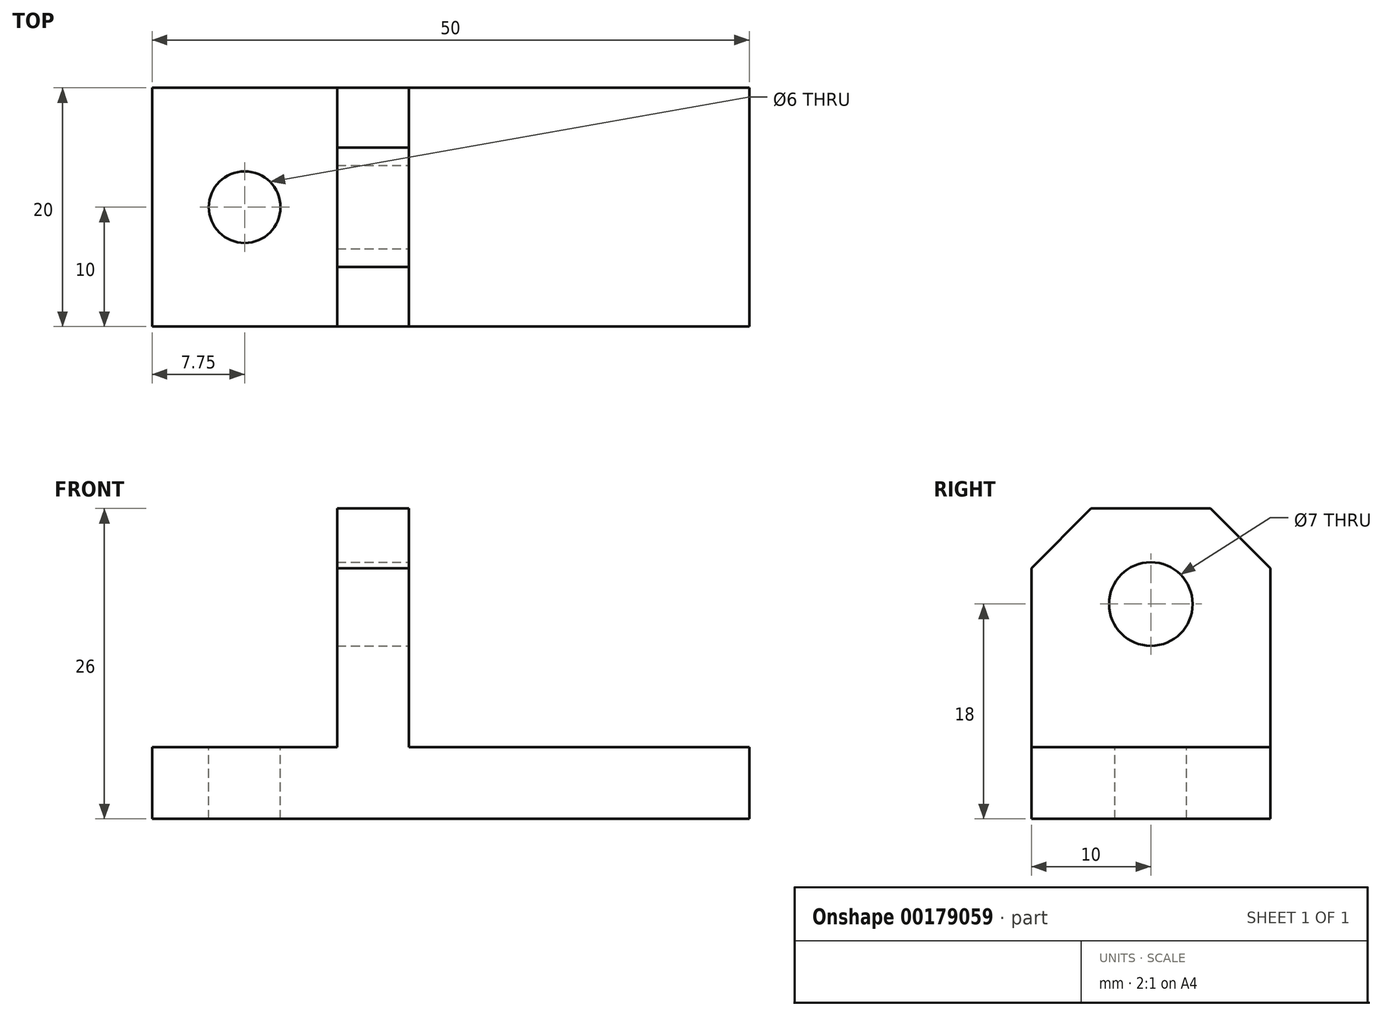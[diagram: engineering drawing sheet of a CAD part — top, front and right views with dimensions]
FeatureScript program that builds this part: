
annotation { "Feature Type Name" : "Feature", "Feature Type Description" : "" }
export const myFeature = defineFeature(function(context is Context, id is Id, definition is map)
    precondition{}
    {
        {
            var Q0;
            Q0=qCreatedBy(makeId("Top.planeOp"),FACE);
            var sketch = newSketch(context, id + "F0", { "sketchPlane" : qUnion([Q0])});
            skLineSegment(sketch, "E0.bottom", {"start": v(25, -10) * mm, "end": v(-25, -10) * mm});
            skLineSegment(sketch, "E0.top", {"start": v(25, 10) * mm, "end": v(-25, 10) * mm});
            skLineSegment(sketch, "E0.left", {"start": v(25, -10) * mm, "end": v(25, 10) * mm});
            skLineSegment(sketch, "E0.right", {"start": v(-25, -10) * mm, "end": v(-25, 10) * mm});
            skPoint(sketch, "E0.middle", {"position": v(0, 0) * mm});
            skSolve(sketch);
        }
        {
            var Q0;
            Q0 = qSketchRegion(id + "F0", true);
            extrude(context, id + "F1", {"entities" : qUnion([Q0]), "depth" : 6 * mm});
        }
        {
            var Q0;
            Q0=makeQuery(id+"F1.opExtrude","CAP_FACE",FACE,{"disambiguationData":[OSD([sQuery(id+"F0.wireOp",EDGE,"E0.bottom"),sQuery(id+"F0.wireOp",EDGE,"E0.top"),sQuery(id+"F0.wireOp",EDGE,"E0.left"),sQuery(id+"F0.wireOp",EDGE,"E0.right")])],"isStart":false});
            var sketch = newSketch(context, id + "F2", { "sketchPlane" : qUnion([Q0])});
            skLineSegment(sketch, "E1", {"start": v(0, 10) * mm, "end": v(0, -10) * mm, "construction": true});
            skLineSegment(sketch, "E2.bottom", {"start": v(-9.5, 10) * mm, "end": v(-3.5, 10) * mm});
            skLineSegment(sketch, "E2.top", {"start": v(-9.5, -10) * mm, "end": v(-3.5, -10) * mm});
            skLineSegment(sketch, "E2.left", {"start": v(-9.5, 10) * mm, "end": v(-9.5, -10) * mm});
            skLineSegment(sketch, "E2.right", {"start": v(-3.5, 10) * mm, "end": v(-3.5, -10) * mm});
            skSolve(sketch);
        }
        {
            var Q0;
            Q0 = qSketchRegion(id + "F2", true);
            extrude(context, id + "F3", {"entities" : qUnion([Q0]), "operationType" : NewBodyOperationType.ADD, "depth" : 20 * mm});
        }
        {
            var Q0;
            Q0=makeQuery(id+"F3.opExtrude","SWEPT_FACE",FACE,{"disambiguationData":[OSD([sQuery(id+"F2.wireOp",EDGE,"E2.right")])]});
            var sketch = newSketch(context, id + "F4", { "sketchPlane" : qUnion([Q0])});
            skLineSegment(sketch, "E3", {"start": v(0, 26) * mm, "end": v(0, 6) * mm, "construction": true});
            skCircle(sketch, "E4", {"center": v(0, 18) * mm, "radius": 3.5 * mm});
            skSolve(sketch);
        }
        {
            var Q0;
            Q0 = qSketchRegion(id + "F4", true);
            extrude(context, id + "F5", {"entities" : qUnion([Q0]), "operationType" : NewBodyOperationType.REMOVE, "oppositeDirection" : true, "depth" : 25 * mm});
        }
        {
            var Q0;
            Q0=makeQuery(id+"F3.opExtrude","CAP_EDGE",EDGE,{"disambiguationData":[OSD([sQuery(id+"F2.wireOp",EDGE,"E2.top")])],"isStart":false});
            var Q1;
            Q1=makeQuery(id+"F3.opExtrude","CAP_EDGE",EDGE,{"disambiguationData":[OSD([sQuery(id+"F2.wireOp",EDGE,"E2.bottom")])],"isStart":false});
            chamfer(context, id + "F6", {"entities" : qUnion([Q0, Q1]), "width" : 5 * mm, "tangentPropagation" : true});
        }
        {
            var Q0;
            {var subQ0=sQuery(id+"F0.wireOp",EDGE,"E0.right");var subQ1=sQuery(id+"F0.wireOp",EDGE,"E0.top");var subQ2=sQuery(id+"F0.wireOp",EDGE,"E0.bottom");Q0=makeQuery(id+"F3.boolean.opBoolean","SPLIT",FACE,{"disambiguationData":[TD([makeQuery(id+"F1.opExtrude","SWEPT_FACE",FACE,{"disambiguationData":[OSD([subQ0])]})])],"derivedFrom":makeQuery(id+"F1.opExtrude","CAP_FACE",FACE,{"disambiguationData":[OSD([subQ2,subQ1,sQuery(id+"F0.wireOp",EDGE,"E0.left"),subQ0])],"isStart":false})});}
            var sketch = newSketch(context, id + "F7", { "sketchPlane" : qUnion([Q0])});
            skLineSegment(sketch, "E5", {"start": v(-25, 0) * mm, "end": v(-9.5, 0) * mm, "construction": true});
            skLineSegment(sketch, "E6", {"start": v(-17.25, 10) * mm, "end": v(-17.25, -10) * mm, "construction": true});
            skCircle(sketch, "E7", {"center": v(-17.25, 0) * mm, "radius": 3 * mm});
            skSolve(sketch);
        }
        {
            var Q0;
            Q0 = qSketchRegion(id + "F7", true);
            extrude(context, id + "F8", {"entities" : qUnion([Q0]), "operationType" : NewBodyOperationType.REMOVE, "oppositeDirection" : true, "depth" : 25 * mm});
        }
    });
